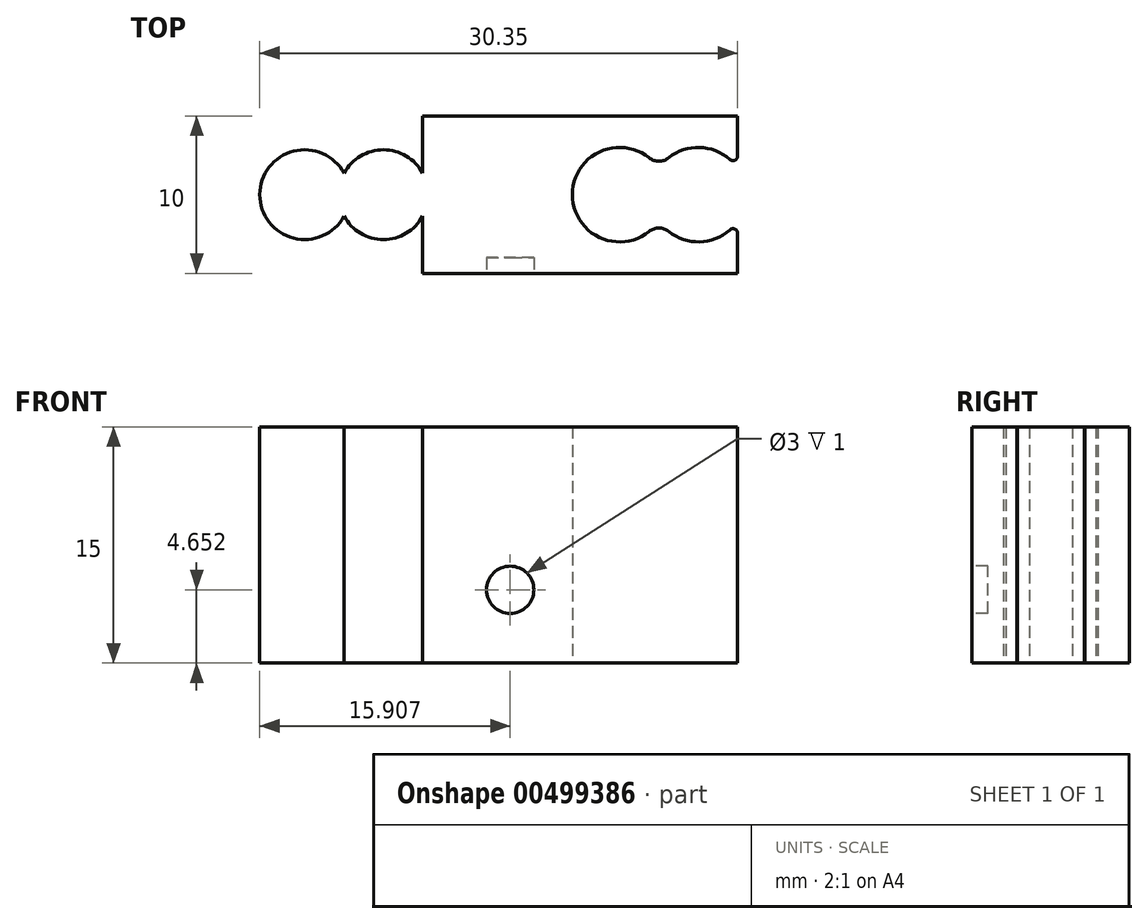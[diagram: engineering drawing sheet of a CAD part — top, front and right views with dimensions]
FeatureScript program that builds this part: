
annotation { "Feature Type Name" : "Feature", "Feature Type Description" : "" }
export const myFeature = defineFeature(function(context is Context, id is Id, definition is map)
    precondition{}
    {
        {
            var Q0;
            Q0=qCreatedBy(makeId("Top.planeOp"),FACE);
            var sketch = newSketch(context, id + "F0", { "sketchPlane" : qUnion([Q0])});
            skLineSegment(sketch, "E0", {"start": v(-28.89, 0) * mm, "end": v(20.55, 0) * mm, "construction": true});
            skLineSegment(sketch, "E1", {"start": v(0, 15.76) * mm, "end": v(0, -17.69) * mm, "construction": true});
            skLineSegment(sketch, "E2.bottom", {"start": v(10, -5) * mm, "end": v(-10, -5) * mm});
            skLineSegment(sketch, "E2.top", {"start": v(10, 5) * mm, "end": v(-10, 5) * mm});
            skLineSegment(sketch, "E2.left", {"start": v(10, -5) * mm, "end": v(10, -2.46) * mm});
            skPoint(sketch, "E2.middle", {"position": v(0, 0) * mm});
            skArc(sketch, "E3", {"start": v(5.62, -2.34) * mm, "mid": v(7.58, -3) * mm, "end": v(9.5, -2.24) * mm});
            skArc(sketch, "E4", {"start": v(4.37, 2.34) * mm, "mid": v(-0.5, 0) * mm, "end": v(4.37, -2.34) * mm});
            skArc(sketch, "E5.trimOffspring", {"start": v(9.5, 2.24) * mm, "mid": v(7.58, 3) * mm, "end": v(5.62, 2.34) * mm});
            skLineSegment(sketch, "E6.trimOffspring", {"start": v(10, 2.46) * mm, "end": v(10, 5) * mm});
            skPoint(sketch, "E7.visualSharp", {"position": v(5, 1.66) * mm});
            skArc(sketch, "E7.filletArc", {"start": v(4.37, 2.34) * mm, "mid": v(5, 2.12) * mm, "end": v(5.62, 2.34) * mm});
            skPoint(sketch, "E8.visualSharp", {"position": v(5, -1.66) * mm});
            skArc(sketch, "E8.filletArc", {"start": v(5.62, -2.34) * mm, "mid": v(5, -2.12) * mm, "end": v(4.37, -2.34) * mm});
            skPoint(sketch, "E9.visualSharp", {"position": v(10, 1.66) * mm});
            skArc(sketch, "E9.filletArc", {"start": v(9.5, 2.24) * mm, "mid": v(9.82, 2.19) * mm, "end": v(10, 2.46) * mm});
            skPoint(sketch, "E10.visualSharp", {"position": v(10, -1.66) * mm});
            skArc(sketch, "E10.filletArc", {"start": v(10, -2.46) * mm, "mid": v(9.82, -2.19) * mm, "end": v(9.5, -2.24) * mm});
            skLineSegment(sketch, "E11.trimOffspring", {"start": v(-10, -5) * mm, "end": v(-10, -1.37) * mm});
            skLineSegment(sketch, "E12.direction1", {"start": v(-28.89, 0) * mm, "end": v(11.11, 0) * mm, "construction": true});
            skArc(sketch, "E13", {"start": v(-15, -1.37) * mm, "mid": v(-12.5, -2.85) * mm, "end": v(-10, -1.37) * mm});
            skArc(sketch, "E14", {"start": v(-15, 1.37) * mm, "mid": v(-20.35, 0) * mm, "end": v(-15, -1.37) * mm});
            skArc(sketch, "E15.trimOffspring", {"start": v(-10, 1.37) * mm, "mid": v(-12.5, 2.85) * mm, "end": v(-15, 1.37) * mm});
            skLineSegment(sketch, "E16.trimOffspring", {"start": v(-10, 1.37) * mm, "end": v(-10, 5) * mm});
            skSolve(sketch);
        }
        {
            var Q0;
            Q0=makeQuery(id+"F0.imprint","IMPRINT",FACE,{"disambiguationData":[TD([[makeQuery(id+"F0.imprint","IMPRINT",EDGE,{"derivedFrom":sQuery(id+"F0.wireOp",EDGE,"E2.bottom")}),-1.0]])]});
            extrude(context, id + "F1", {"entities" : qUnion([Q0]), "depth" : 15 * mm});
        }
        {
            var Q0;
            Q0=makeQuery(id+"F1.opExtrude","SWEPT_FACE",FACE,{"disambiguationData":[OSD([sQuery(id+"F0.wireOp",EDGE,"E2.bottom")])]});
            var sketch = newSketch(context, id + "F2", { "sketchPlane" : qUnion([Q0])});
            skCircle(sketch, "E17", {"center": v(-4.44, 4.65) * mm, "radius": 1.5 * mm});
            skSolve(sketch);
        }
        {
            var Q0;
            Q0=makeQuery(id+"F2.imprint","IMPRINT",FACE,{"disambiguationData":[TD([[makeQuery(id+"F2.imprint","IMPRINT",EDGE,{"derivedFrom":sQuery(id+"F2.wireOp",EDGE,"E17")}),1.0]])]});
            extrude(context, id + "F3", {"entities" : qUnion([Q0]), "operationType" : NewBodyOperationType.REMOVE, "oppositeDirection" : true, "depth" : 1 * mm});
        }
    });
